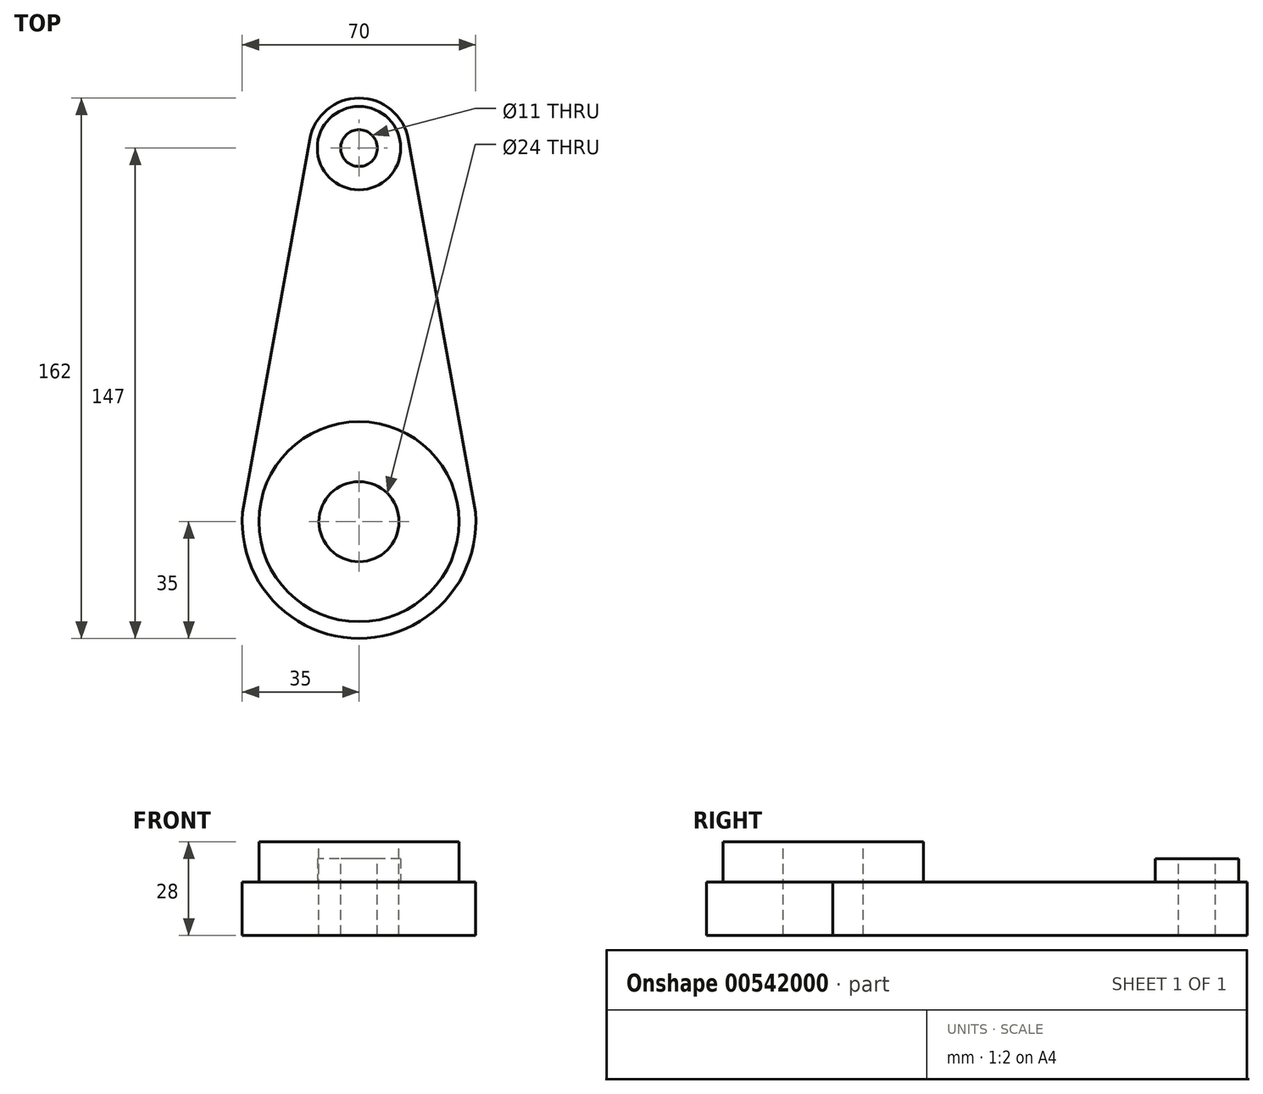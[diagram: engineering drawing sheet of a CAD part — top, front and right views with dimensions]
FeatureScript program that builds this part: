
annotation { "Feature Type Name" : "Feature", "Feature Type Description" : "" }
export const myFeature = defineFeature(function(context is Context, id is Id, definition is map)
    precondition{}
    {
        {
            var Q0;
            Q0=qCreatedBy(makeId("Top.planeOp"),FACE);
            var sketch = newSketch(context, id + "F0", { "sketchPlane" : qUnion([Q0])});
            skArc(sketch, "E0", {"start": v(-33.67, 9.56) * mm, "mid": v(-3.45, -34.83) * mm, "end": v(34.89, 2.78) * mm});
            skArc(sketch, "E1", {"start": v(14.76, 114.66) * mm, "mid": v(0, 127) * mm, "end": v(-14.76, 114.66) * mm});
            skLineSegment(sketch, "E2", {"start": v(34.89, 2.78) * mm, "end": v(14.76, 114.66) * mm});
            skLineSegment(sketch, "E3", {"start": v(-34.89, 2.78) * mm, "end": v(-14.76, 114.66) * mm});
            skSolve(sketch);
        }
        {
            var Q0;
            {var subQ5=sQuery(id+"F0.wireOp",EDGE,"E1");Q0=makeQuery(id+"F0.imprint","IMPRINT",FACE,{"disambiguationData":[TD([[makeQuery(id+"F0.imprint","IMPRINT",EDGE,{"derivedFrom":subQ5}),1.0]])]});}
            extrude(context, id + "F1", {"entities" : qUnion([Q0]), "depth" : 16 * mm, "offsetDistance" : 25.4 * mm});
        }
        {
            var Q0;
            Q0=makeQuery(id+"F1.opExtrude","CAP_FACE",FACE,{"disambiguationData":[OSD([sQuery(id+"F0.wireOp",EDGE,"E0"),sQuery(id+"F0.wireOp",EDGE,"E1"),sQuery(id+"F0.wireOp",EDGE,"E2"),sQuery(id+"F0.wireOp",EDGE,"E3")])],"isStart":false});
            var sketch = newSketch(context, id + "F2", { "sketchPlane" : qUnion([Q0])});
            skCircle(sketch, "E4", {"center": v(0, 0) * mm, "radius": 30 * mm});
            skCircle(sketch, "E5", {"center": v(0, 112) * mm, "radius": 12.5 * mm});
            skSolve(sketch);
        }
        {
            var Q0;
            Q0=makeQuery(id+"F2.imprint","IMPRINT",FACE,{"disambiguationData":[TD([[makeQuery(id+"F2.imprint","IMPRINT",EDGE,{"derivedFrom":sQuery(id+"F2.wireOp",EDGE,"E5")}),1.0]])]});
            var Q1;
            Q1=makeQuery(id+"F2.imprint","IMPRINT",FACE,{"disambiguationData":[TD([[makeQuery(id+"F2.imprint","IMPRINT",EDGE,{"derivedFrom":sQuery(id+"F2.wireOp",EDGE,"E4")}),1.0]])]});
            extrude(context, id + "F3", {"entities" : qUnion([Q0, Q1]), "operationType" : NewBodyOperationType.ADD, "depth" : 12 * mm, "offsetDistance" : 25.4 * mm});
        }
        {
            var Q0;
            Q0=makeQuery(id+"F3.opExtrude","CAP_FACE",FACE,{"disambiguationData":[OSD([sQuery(id+"F2.wireOp",EDGE,"E4")])],"isStart":false});
            var sketch = newSketch(context, id + "F4", { "sketchPlane" : qUnion([Q0])});
            skPoint(sketch, "E6", {"position": v(0, 0) * mm});
            skSolve(sketch);
        }
        {
            var Q0;
            Q0=sQuery(id+"F4.wireOp",VERTEX,"E6");
            var Q1;
            Q1=makeQuery(id+"F1.opExtrude","SWEPT_BODY",BODY,{"disambiguationData":[OSD([sQuery(id+"F0.wireOp",EDGE,"E0"),sQuery(id+"F0.wireOp",EDGE,"E1"),sQuery(id+"F0.wireOp",EDGE,"E2"),sQuery(id+"F0.wireOp",EDGE,"E3")])]});
            hole(context, id + "F5", {"style" : HoleStyle.SIMPLE, "endStyle" : HoleEndStyle.THROUGH, "holeDiameter" : 24 * mm, "isTappedThrough" : true, "tappedDepth" : 12.7 * mm, "tapClearance" : 3, "locations" : qUnion([Q0]), "scope" : qUnion([Q1])});
        }
        {
            var Q0;
            Q0=makeQuery(id+"F3.opExtrude","CAP_FACE",FACE,{"disambiguationData":[OSD([sQuery(id+"F2.wireOp",EDGE,"E5")])],"isStart":false});
            var sketch = newSketch(context, id + "F6", { "sketchPlane" : qUnion([Q0])});
            skPoint(sketch, "E7", {"position": v(0, 112) * mm});
            skSolve(sketch);
        }
        {
            var Q0;
            Q0=sQuery(id+"F6.wireOp",VERTEX,"E7");
            var Q1;
            Q1=makeQuery(id+"F1.opExtrude","SWEPT_BODY",BODY,{"disambiguationData":[OSD([sQuery(id+"F0.wireOp",EDGE,"E0"),sQuery(id+"F0.wireOp",EDGE,"E1"),sQuery(id+"F0.wireOp",EDGE,"E2"),sQuery(id+"F0.wireOp",EDGE,"E3")])]});
            hole(context, id + "F7", {"style" : HoleStyle.SIMPLE, "endStyle" : HoleEndStyle.THROUGH, "holeDiameter" : 11 * mm, "isTappedThrough" : true, "tappedDepth" : 12.7 * mm, "tapClearance" : 3, "locations" : qUnion([Q0]), "scope" : qUnion([Q1])});
        }
        {
            var Q0;
            Q0=makeQuery(id+"F3.opExtrude","CAP_FACE",FACE,{"disambiguationData":[OSD([sQuery(id+"F2.wireOp",EDGE,"E5")])],"isStart":false});
            var sketch = newSketch(context, id + "F8", { "sketchPlane" : qUnion([Q0])});
            skCircle(sketch, "E8.0.0", {"center": v(0, 112) * mm, "radius": 12.5 * mm});
            skSolve(sketch);
        }
        {
            var Q0;
            Q0 = qSketchRegion(id + "F8", true);
            extrude(context, id + "F9", {"entities" : qUnion([Q0]), "operationType" : NewBodyOperationType.REMOVE, "oppositeDirection" : true, "depth" : 5 * mm, "offsetDistance" : 25.4 * mm});
        }
    });
